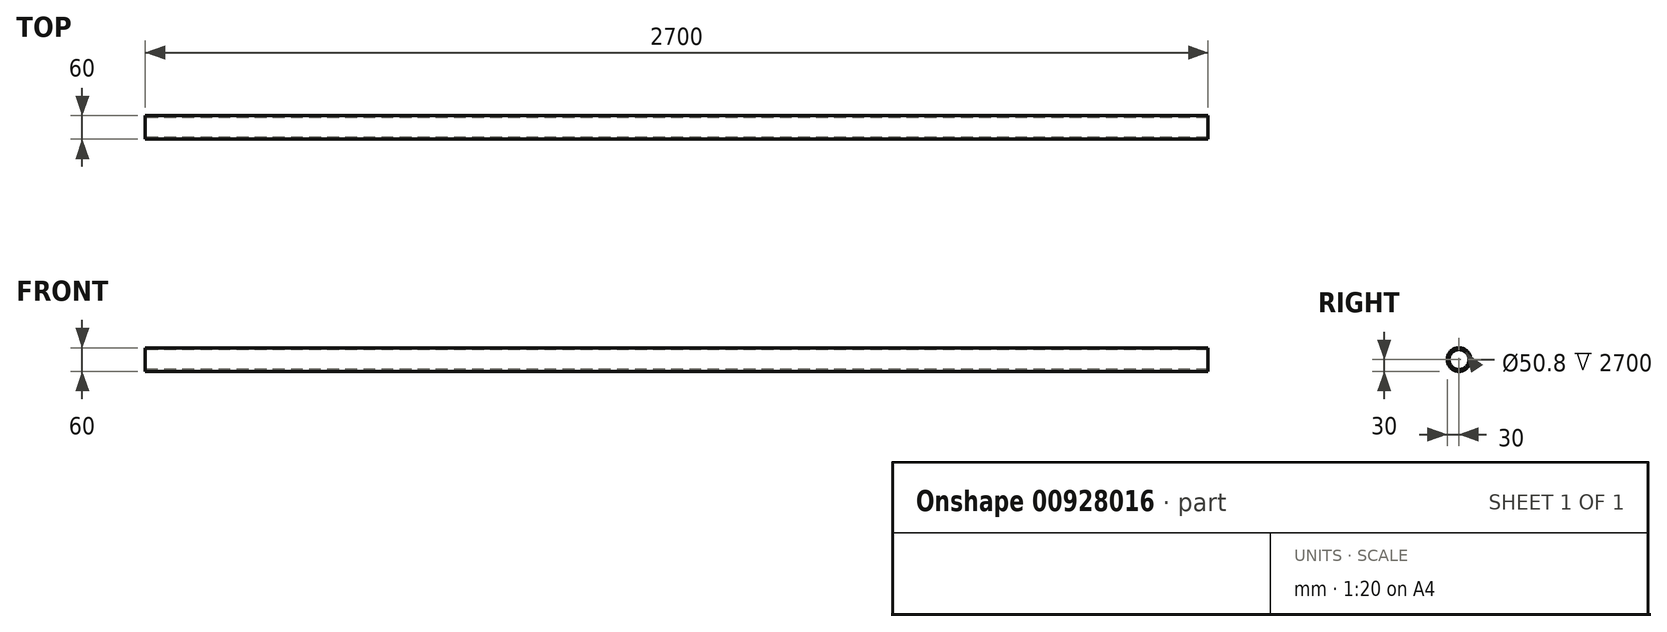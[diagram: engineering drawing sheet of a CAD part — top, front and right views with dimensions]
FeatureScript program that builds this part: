
annotation { "Feature Type Name" : "Feature", "Feature Type Description" : "" }
export const myFeature = defineFeature(function(context is Context, id is Id, definition is map)
    precondition{}
    {
        {
            var Q0;
            Q0=qCreatedBy(makeId("Right.planeOp"),FACE);
            var sketch = newSketch(context, id + "F0", { "sketchPlane" : qUnion([Q0])});
            skCircle(sketch, "E0", {"center": v(0, 0) * mm, "radius": 30 * mm});
            skCircle(sketch, "E1", {"center": v(0, 0) * mm, "radius": 25.4 * mm});
            skSolve(sketch);
        }
        {
            var Q0;
            Q0=qSketchRegion(id+"F0",true);
            extrude(context, id + "F1", {"entities" : qUnion([Q0]), "depth" : 2700 * mm, "offsetDistance" : 25 * mm});
        }
    });
